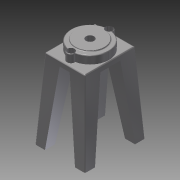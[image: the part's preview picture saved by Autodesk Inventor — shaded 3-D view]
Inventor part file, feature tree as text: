
AUTODESK INVENTOR PART (.ipt)
format: ipt  version: 2015 (Build 190159000, 159)  size: 252,416 bytes
history: native  units: in
note: dims shown in document units (in); Inventor stores cm internally (conversion verified against a paired STEP export)
features: extrude x6, sketch x6, chamfer x4, fillet x4
ambient origin geometry x8: Origin, YZ Plane, XZ Plane, XY Plane, X Axis, Y Axis, Z Axis, Center Point
bodies: Solid1 (feature_tree)
feature tree (20):
  extrude  "Extrusion1"  TaperAngle=0.0deg  [1 undecoded]
  extrude  "Extrusion2"  Depth=3.937in
  chamfer  "Chamfer1"  Distance=7.874in
  chamfer  "Chamfer2"  Distance=7.874in
  chamfer  "Chamfer3"  Distance=19.685in
  chamfer  "Chamfer4"  Distance=3.937in
  fillet  "Fillet1"  Radius=3.937in
  extrude  "Extrusion3"  Depth=0.3937in
  fillet  "Fillet2"  Radius=29.5276in
  extrude  "Extrusion4"  Depth=0.3937in
  fillet  "Fillet3"  Radius=3.937in
  extrude  "Extrusion5"  Depth=0.3937in TaperAngle=0.0deg
  fillet  "Fillet4"  Radius=1.9685in
  extrude  "Extrusion6"  Depth=0.3937in TaperAngle=45.0deg
  sketch  "Sketch1"  dims[d4=3.937in d5=0.0in]
  sketch  "Sketch4"  dims[d6=31.4961in d7=3.937in]
  sketch  "Sketch5"  dims[d8=0.0in]
  sketch  "Sketch6"  dims[d9=31.4961in]
  sketch  "Sketch7"  dims[d10=1.9685in]
  sketch  "Sketch8"  dims[d11=7.874in d12=7.874in d13=7.874in d14=19.685in d15=0.0in d16=3.937in d17=3.937in d18=3.937in d19=29.5276in d20=3.937in d21=3.937in d22=23.622in d23=0.0in d24=1.9685in d25=31.4961in d26=45.0deg d27=1.9685in d28=31.4961in d29=45.0deg d30=1.9685in d31=31.4961in d32=45.0deg d33=1.9685in d34=31.4961in d35=45.0deg d36=0.3937in d37=14.9606in d38=9.8425in d39=9.8425in d40=3.1496in d41=3.1496in d42=3.1496in d43=0.0in d44=0.5906in d45=2.7559in d46=2.7559in d47=1.9685in d48=0.0in d49=0.3937in d50=11.4173in d51=0.3937in d52=0.0in d53=0.3937in d54=3.1496in d55=0.3937in d56=0.0in]
note: 1 required parameter value undecoded (feature->parameter linkage not recoverable at this tier; creation-order binding heuristic only, values carry confidence <= 0.55)
